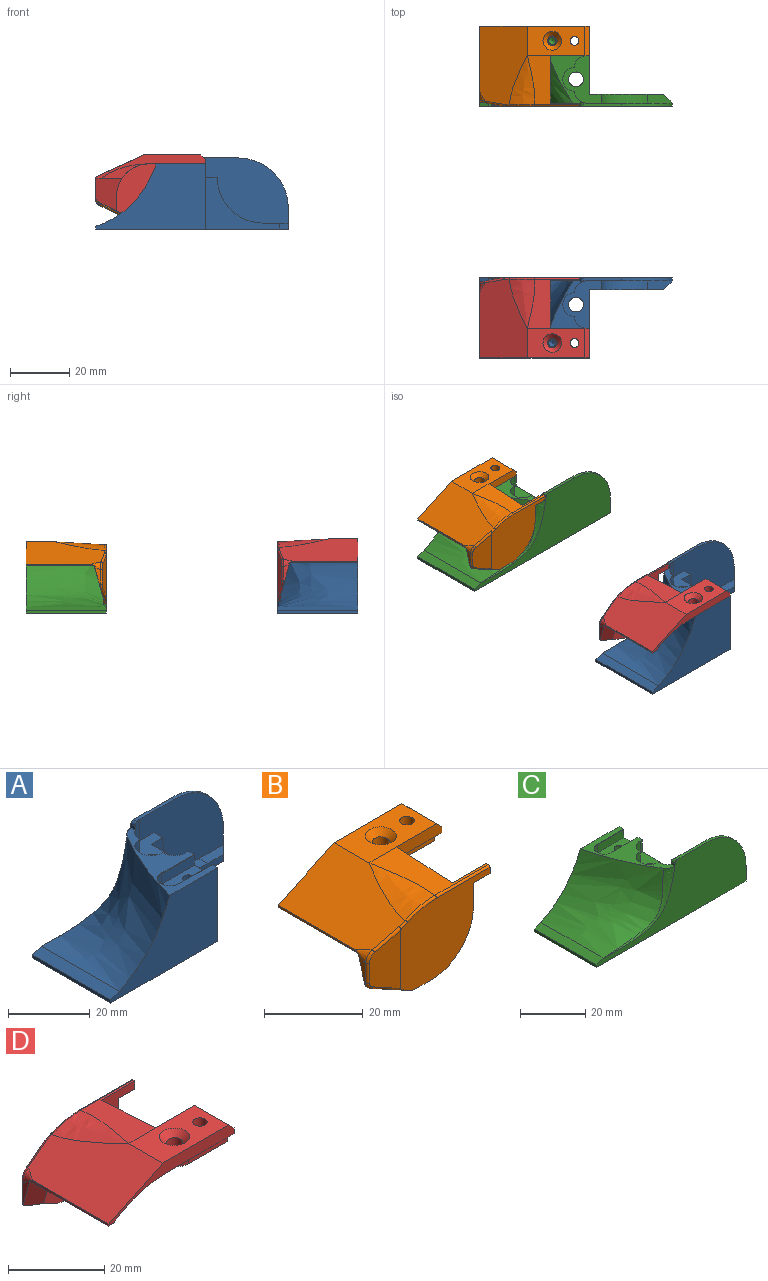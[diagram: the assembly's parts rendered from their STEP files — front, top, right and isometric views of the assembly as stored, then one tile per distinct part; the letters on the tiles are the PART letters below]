
ASSEMBLY  parts=4 mates=3
PART A: 37 faces, bbox 65.1x72.7x39.1 mm
  f0: plane 27.06x16.59mm, normal (0,0,1), area 125.5mm2, adj f3,f4,f10,f12,f14,f15,f16,f21
  f1: cylinder r=1.5mm len=18.8mm, axis (0,0,1), area 177.2mm2, adj f9,f26
  f2: plane 25x17.5mm, normal (0,-1,0), area 163.6mm2, adj f3,f9,f11,f17,f18,f19
  f3: plane 23x22mm, normal (1,0,0), area 428.3mm2, adj f0,f2,f4,f9,f11,f12,f26,f27
  f4: plane 37x22mm, normal (0,-1,0), area 528.7mm2, adj f0,f3,f7,f9,f21,f22
  f5: plane 65x24mm, normal (0,1,0), area 817.9mm2, adj f6,f7,f8,f9,f20,f22,f24,f25
  f6: plane 7x1mm, normal (1,0,0), area 7mm2, adj f5,f9,f13,f19,f20
  f7: plane 27x0.91mm, normal (-1,0,0), area 24.5mm2, adj f4,f5,f9,f22
  f8: plane 13x1.13mm, normal (0,0,1), area 13mm2, adj f5,f13,f14,f20,f25
  f9: plane 65x27mm, normal (0,0,-1), area 1079.8mm2, adj f1,f2,f3,f4,f5,f6,f7,f19
  f10: plane 1.54x1.01mm, normal (-1,0,0), area 1.5mm2, adj f0,f14,f24,f25
  f11: plane 16x13mm, normal (0,0,1), area 90.6mm2, adj f2,f3,f12,f13,f14,f15,f16,f17
  f12: plane 4.5x1mm, normal (0,1,0), area 4.5mm2, adj f0,f3,f11,f16
  f13: plane 29x22mm, normal (0,-1,0), area 446.9mm2, adj f6,f8,f11,f14,f17,f18,f20
  f14: cylinder r=4mm len=6.5mm, axis (0,0,1), area 31.9mm2, adj f0,f8,f10,f11,f13,f15,f25
  f15: cylinder r=4mm len=8mm, axis (0,0,1), area 56.5mm2, adj f0,f11,f14,f16
  f16: cylinder r=4mm len=4.5mm, axis (0,0,1), area 28.3mm2, adj f0,f11,f12,f15
  f17: cylinder r=15.5mm len=15.5mm, axis (0,-1,0), area 73mm2, adj f2,f11,f13,f18
  f18: plane 8.5x3mm, normal (0,0,1), area 21mm2, adj f2,f13,f17,f19
  f19: plane 3x3mm, normal (0.71,-0.71,0), area 8.5mm2, adj f2,f6,f9,f18
  f20: cylinder r=17mm len=17mm, axis (0,-1,0), area 26.7mm2, adj f5,f6,f8,f13
  f21: bspline ~72.59x37mm, area 910.9mm2, adj f0,f4,f22,f24
  f22: plane 27x3mm, normal (-0.34,0,0.94), area 86.2mm2, adj f4,f5,f7,f21
  f23: cylinder r=2.5mm len=17.5mm, axis (0,0,-1), area 274.9mm2, adj f9,f11
  f24: bspline ~31.79x24.78mm, area 59.9mm2, adj f0,f5,f10,f21,f25
  f25: cylinder r=1mm len=1.54mm, axis (0,-1,0), area 2.1mm2, adj f5,f8,f10,f14,f24
  f26: plane 14.5x6mm, normal (0,0,1), area 69mm2, adj f1,f3,f27,f28,f29,f33
  f27: plane 11.5x3.1mm, normal (0,1,0), area 35.6mm2, adj f3,f26,f29,f36
  f28: plane 11.5x3.1mm, normal (0,-1,0), area 35.6mm2, adj f3,f26,f29,f34
  f29: cylinder r=3mm len=6mm, axis (0,0,1), area 29.2mm2, adj f26,f27,f28,f35
  f30: cone r=1.25mm half-angle=59deg, axis (0,0,1), area 5.7mm2, adj f31
  f31: cylinder r=1.25mm len=2.5mm, axis (0,0,1), area 11.8mm2, adj f30,f32
  f32: plane 3x3mm, normal (0,0,1), area 2.2mm2, adj f31,f33
  f33: cylinder r=1.5mm len=3mm, axis (0,0,1), area 26.4mm2, adj f26,f32
  f34: plane 11.5x0.1mm, normal (0,-0.71,0.71), area 1.6mm2, adj f0,f3,f28,f35
  f35: cone r=3mm half-angle=45deg, axis (0,0,1), area 1.4mm2, adj f0,f29,f34,f36
  f36: plane 11.5x0.1mm, normal (0,0.71,0.71), area 1.6mm2, adj f0,f3,f27,f35
PART B: 47 faces, bbox 40x32.5x24 mm
  f0: plane 26x19.53mm, normal (0,0,-1), area 215.1mm2, adj f9,f10,f12,f14,f15,f17,f18,f19
  f1: plane 4.8x1mm, normal (0,0,-1), area 4.8mm2, adj f3,f11,f17,f34
  f2: plane 9.78x4.56mm, normal (-0.42,0,-0.91), area 3.7mm2, adj f17,f20,f30,f39
  f3: plane 6x1mm, normal (1,0,0), area 6mm2, adj f1,f4,f11,f17
  f4: cylinder r=12mm len=12mm, axis (0,-1,0), area 18.8mm2, adj f3,f5,f11,f17
  f5: plane 4.54x1mm, normal (0,0,-1), area 4.5mm2, adj f4,f11,f17,f39
  f6: plane 25.33x6.84mm, normal (-1,0,0), area 16.4mm2, adj f10,f13,f20,f23,f24,f28
  f7: plane 29.72x19.07mm, normal (-0.42,0,0.91), area 394.5mm2, adj f8,f10,f24,f25,f26,f37
  f8: plane 19.42x10mm, normal (0,0,1), area 155.9mm2, adj f7,f10,f19,f22,f31,f32,f35
  f9: plane 10x4.5mm, normal (1,0,0), area 33mm2, adj f0,f10,f19,f35,f41,f42,f43,f44
  f10: plane 37x8mm, normal (0,1,0), area 82.6mm2, adj f0,f6,f7,f8,f9,f12,f13,f35
  f11: plane 25.81x19.54mm, normal (0,-1,0), area 372.6mm2, adj f1,f3,f4,f5,f21,f26,f30,f34
  f12: cylinder r=28mm len=23mm, axis (0,1,0), area 390.8mm2, adj f0,f10,f13,f14
  f13: plane 23x1.5mm, normal (0,0,-1), area 34.5mm2, adj f6,f10,f12,f20
  f14: plane 16.5x5mm, normal (0,1,0), area 24.4mm2, adj f0,f12,f15,f20
  f15: cylinder r=11mm len=11mm, axis (0,1,0), area 46.5mm2, adj f0,f14,f16,f17,f20
  f16: plane 4.76x1.33mm, normal (1,0,0), area 3.2mm2, adj f15,f17,f20
  f17: plane 26.8x20.06mm, normal (0,1,0), area 353.9mm2, adj f0,f1,f2,f3,f4,f5,f15,f16
  f18: plane 16x3mm, normal (1,0,0), area 40.5mm2, adj f0,f17,f19,f22
  f19: plane 13x3mm, normal (0,-1,0), area 37.9mm2, adj f0,f8,f9,f18,f35
  f20: plane 10.84x8.85mm, normal (0,0.96,-0.27), area 69.6mm2, adj f2,f6,f13,f14,f15,f16,f23,f29
  f21: plane 14.23x7.5mm, normal (-0.17,-0.98,0), area 81.3mm2, adj f11,f26,f27,f28,f29,f30
  f22: plane 20.86x19.67mm, normal (0,-0.06,1), area 108.9mm2, adj f8,f17,f18,f25,f34,f36
  f23: cylinder r=2mm len=1.63mm, axis (0,-1,0), area 0.3mm2, adj f6,f20,f29
  f24: bspline ~25.59x2.72mm, area 5.2mm2, adj f6,f7,f27
  f25: bspline ~19.5x9.41mm, area 58.1mm2, adj f7,f22,f38
  f26: cylinder r=0.6mm len=6.82mm, axis (-0.89,0.16,-0.42), area 6.5mm2, adj f7,f11,f21,f27,f37
  f27: bspline ~2.7x1.97mm, area 2.5mm2, adj f21,f24,f26,f28
  f28: cylinder r=0.6mm len=4.9mm, axis (0,0,-1), area 4.1mm2, adj f6,f21,f27,f29
  f29: bspline ~2.23x1.42mm, area 1.7mm2, adj f20,f21,f23,f28,f30
  f30: cylinder r=0.6mm len=10.2mm, axis (0.89,-0.16,-0.42), area 8mm2, adj f2,f11,f20,f21,f29,f39
  f31: cylinder r=1.5mm len=6mm, axis (0,0,1), area 56.5mm2, adj f8,f43
  f32: cone r=3.15mm half-angle=45deg, axis (0,0,1), area 31.2mm2, adj f8,f33
  f33: cylinder r=1.7mm len=4.55mm, axis (0,0,1), area 48.6mm2, adj f32,f43
  f34: plane 2.06x1mm, normal (1,0,0), area 2mm2, adj f1,f11,f17,f22,f36
  f35: plane 10x1.5mm, normal (0.71,0,0.71), area 21.2mm2, adj f8,f9,f10,f19
  f36: cylinder r=0.5mm len=15.32mm, axis (-1,0,0), area 11.6mm2, adj f11,f22,f34,f38
  f37: cylinder r=0.5mm len=2.32mm, axis (-0.91,0,-0.42), area 1.6mm2, adj f7,f11,f26,f38
  f38: bspline ~8.57x2.36mm, area 6.8mm2, adj f11,f25,f36,f37
  f39: cylinder r=3mm len=1.27mm, axis (0,-1,0), area 1.3mm2, adj f2,f5,f11,f17,f30
  f40: cylinder r=3mm len=6mm, axis (0,0,1), area 27.3mm2, adj f0,f41,f42,f45
  f41: plane 11.5x2.9mm, normal (0,1,0), area 33.3mm2, adj f0,f9,f40,f44
  f42: plane 11.5x2.9mm, normal (0,-1,0), area 33.3mm2, adj f0,f9,f40,f46
  f43: plane 14.4x5.8mm, normal (0,0,-1), area 63.8mm2, adj f9,f31,f33,f44,f45,f46
  f44: plane 11.5x0.1mm, normal (0,0.71,-0.71), area 1.6mm2, adj f9,f41,f43,f45
  f45: cone r=2.9mm half-angle=45deg, axis (0,0,1), area 1.3mm2, adj f40,f43,f44,f46
  f46: plane 11.5x0.1mm, normal (0,-0.71,-0.71), area 1.6mm2, adj f9,f42,f43,f45
PART C: 37 faces, bbox 75.8x83.2x49.7 mm
  f0: cylinder r=1.5mm len=17.8mm, axis (0,0,1), area 167.8mm2, adj f8,f26
  f1: plane 25x16.5mm, normal (0,1,0), area 159.1mm2, adj f2,f8,f11,f17,f18,f19
  f2: plane 23x21mm, normal (1,0,0), area 405.3mm2, adj f1,f3,f8,f9,f11,f12,f26,f27
  f3: plane 47.79x31.81mm, normal (0,1,0), area 512mm2, adj f2,f6,f8,f9,f21,f22
  f4: plane 65x23mm, normal (0,-1,0), area 785.1mm2, adj f5,f6,f7,f8,f20,f22,f24,f25
  f5: plane 6x1mm, normal (1,0,0), area 6mm2, adj f4,f8,f13,f19,f20
  f6: plane 27x0.91mm, normal (-1,0,0), area 24.5mm2, adj f3,f4,f8,f22
  f7: plane 13x1.13mm, normal (0,0,1), area 13mm2, adj f4,f13,f14,f20,f25
  f8: plane 65x27mm, normal (0,0,-1), area 1079.8mm2, adj f0,f1,f2,f3,f4,f5,f6,f19
  f9: plane 31.5x21.41mm, normal (0,0,1), area 133.6mm2, adj f2,f3,f10,f12,f14,f15,f16,f21
  f10: plane 1.55x1.02mm, normal (-1,0,0), area 1.5mm2, adj f9,f14,f24,f25
  f11: plane 16x13mm, normal (0,0,1), area 90.6mm2, adj f1,f2,f12,f13,f14,f15,f16,f17
  f12: plane 4.5x1mm, normal (0,-1,0), area 4.5mm2, adj f2,f9,f11,f16
  f13: plane 29x21mm, normal (0,1,0), area 423.4mm2, adj f5,f7,f11,f14,f17,f18,f20
  f14: cylinder r=4mm len=6.5mm, axis (0,0,1), area 31.9mm2, adj f7,f9,f10,f11,f13,f15,f25
  f15: cylinder r=4mm len=8mm, axis (0,0,1), area 56.5mm2, adj f9,f11,f14,f16
  f16: cylinder r=4mm len=4.5mm, axis (0,0,1), area 28.3mm2, adj f9,f11,f12,f15
  f17: cylinder r=15.5mm len=15.47mm, axis (0,1,0), area 70mm2, adj f1,f11,f13,f18
  f18: plane 8.53x3mm, normal (0,0,1), area 21.1mm2, adj f1,f13,f17,f19
  f19: plane 3x3mm, normal (0.71,0.71,0), area 8.5mm2, adj f1,f5,f8,f18
  f20: cylinder r=17mm len=17mm, axis (0,1,0), area 26.7mm2, adj f4,f5,f7,f13
  f21: bspline ~72.4x36.9mm, area 726.6mm2, adj f3,f9,f22,f24
  f22: plane 27x3mm, normal (-0.34,0,0.94), area 86.2mm2, adj f3,f4,f6,f21
  f23: cylinder r=2.5mm len=16.5mm, axis (0,0,-1), area 259.2mm2, adj f8,f11
  f24: bspline ~31.68x23.74mm, area 57.8mm2, adj f4,f9,f10,f21,f25
  f25: cylinder r=1mm len=1.54mm, axis (0,1,0), area 2.1mm2, adj f4,f7,f10,f14,f24
  f26: plane 14.5x6mm, normal (0,0,1), area 69mm2, adj f0,f2,f27,f28,f29,f33
  f27: plane 11.5x3.1mm, normal (0,-1,0), area 35.6mm2, adj f2,f26,f28,f34
  f28: cylinder r=3mm len=6mm, axis (0,0,1), area 29.2mm2, adj f26,f27,f29,f35
  f29: plane 11.5x3.1mm, normal (0,1,0), area 35.6mm2, adj f2,f26,f28,f36
  f30: cone r=1.25mm half-angle=59deg, axis (0,0,1), area 5.7mm2, adj f31
  f31: cylinder r=1.25mm len=2.5mm, axis (0,0,1), area 11.8mm2, adj f30,f32
  f32: plane 3x3mm, normal (0,0,1), area 2.2mm2, adj f31,f33
  f33: cylinder r=1.5mm len=3mm, axis (0,0,1), area 26.4mm2, adj f26,f32
  f34: plane 11.5x0.1mm, normal (0,-0.71,0.71), area 1.6mm2, adj f2,f9,f27,f35
  f35: cone r=3mm half-angle=45deg, axis (0,0,1), area 1.4mm2, adj f9,f28,f34,f36
  f36: plane 11.5x0.1mm, normal (0,0.71,0.71), area 1.6mm2, adj f2,f9,f29,f35
PART D: 47 faces, bbox 40x32.5x24 mm
  f0: plane 4.8x1mm, normal (0,0,-1), area 4.8mm2, adj f2,f11,f17,f34
  f1: plane 9.78x4.56mm, normal (-0.42,0,-0.91), area 3.7mm2, adj f17,f20,f30,f39
  f2: plane 6x1mm, normal (1,0,0), area 6mm2, adj f0,f3,f11,f17
  f3: cylinder r=12mm len=12mm, axis (0,1,0), area 18.8mm2, adj f2,f4,f11,f17
  f4: plane 4.54x1mm, normal (0,0,-1), area 4.5mm2, adj f3,f11,f17,f39
  f5: plane 25.33x6.84mm, normal (-1,0,0), area 16.4mm2, adj f10,f13,f20,f23,f24,f28
  f6: plane 29.72x19.07mm, normal (-0.42,0,0.91), area 394.5mm2, adj f7,f10,f24,f25,f26,f37
  f7: plane 19.42x10mm, normal (0,0,1), area 155.9mm2, adj f6,f10,f19,f22,f31,f32,f35
  f8: plane 10x4.5mm, normal (1,0,0), area 33mm2, adj f9,f10,f19,f35,f40,f42,f43,f44
  f9: plane 26x19.53mm, normal (0,0,-1), area 215.1mm2, adj f8,f10,f12,f14,f15,f17,f18,f19
  f10: plane 37x8mm, normal (0,-1,0), area 82.6mm2, adj f5,f6,f7,f8,f9,f12,f13,f35
  f11: plane 25.81x19.54mm, normal (0,1,0), area 372.6mm2, adj f0,f2,f3,f4,f21,f26,f30,f34
  f12: cylinder r=28mm len=23mm, axis (0,-1,0), area 390.8mm2, adj f9,f10,f13,f14
  f13: plane 23x1.5mm, normal (0,0,-1), area 34.5mm2, adj f5,f10,f12,f20
  f14: plane 16.5x5mm, normal (0,-1,0), area 24.4mm2, adj f9,f12,f15,f20
  f15: cylinder r=11mm len=11mm, axis (0,-1,0), area 46.5mm2, adj f9,f14,f16,f17,f20
  f16: plane 4.76x1.33mm, normal (1,0,0), area 3.2mm2, adj f15,f17,f20
  f17: plane 26.8x20.06mm, normal (0,-1,0), area 353.9mm2, adj f0,f1,f2,f3,f4,f9,f15,f16
  f18: plane 16x3mm, normal (1,0,0), area 40.5mm2, adj f9,f17,f19,f22
  f19: plane 13x3mm, normal (0,1,0), area 37.9mm2, adj f7,f8,f9,f18,f35
  f20: plane 10.84x8.85mm, normal (0,-0.96,-0.27), area 69.6mm2, adj f1,f5,f13,f14,f15,f16,f23,f29
  f21: plane 14.23x7.5mm, normal (-0.17,0.98,0), area 81.3mm2, adj f11,f26,f27,f28,f29,f30
  f22: plane 20.86x19.67mm, normal (0,0.06,1), area 108.9mm2, adj f7,f17,f18,f25,f34,f36
  f23: cylinder r=2mm len=1.63mm, axis (0,1,0), area 0.3mm2, adj f5,f20,f29
  f24: bspline ~25.59x2.72mm, area 5.2mm2, adj f5,f6,f27
  f25: bspline ~19.5x9.41mm, area 58.1mm2, adj f6,f22,f38
  f26: cylinder r=0.6mm len=6.82mm, axis (-0.89,-0.16,-0.42), area 6.5mm2, adj f6,f11,f21,f27,f37
  f27: bspline ~2.7x1.97mm, area 2.5mm2, adj f21,f24,f26,f28
  f28: cylinder r=0.6mm len=4.9mm, axis (0,0,-1), area 4.1mm2, adj f5,f21,f27,f29
  f29: bspline ~2.23x1.42mm, area 1.7mm2, adj f20,f21,f23,f28,f30
  f30: cylinder r=0.6mm len=10.2mm, axis (0.89,0.16,-0.42), area 8mm2, adj f1,f11,f20,f21,f29,f39
  f31: cylinder r=1.5mm len=6mm, axis (0,0,1), area 56.5mm2, adj f7,f43
  f32: cone r=3.15mm half-angle=45deg, axis (0,0,1), area 31.2mm2, adj f7,f33
  f33: cylinder r=1.7mm len=4.55mm, axis (0,0,1), area 48.6mm2, adj f32,f43
  f34: plane 2.06x1mm, normal (1,0,0), area 2mm2, adj f0,f11,f17,f22,f36
  f35: plane 10x1.5mm, normal (0.71,0,0.71), area 21.2mm2, adj f7,f8,f10,f19
  f36: cylinder r=0.5mm len=15.32mm, axis (-1,0,0), area 11.6mm2, adj f11,f22,f34,f38
  f37: cylinder r=0.5mm len=2.32mm, axis (-0.91,0,-0.42), area 1.6mm2, adj f6,f11,f26,f38
  f38: bspline ~8.57x2.36mm, area 6.8mm2, adj f11,f25,f36,f37
  f39: cylinder r=3mm len=1.27mm, axis (0,1,0), area 1.3mm2, adj f1,f4,f11,f17,f30
  f40: plane 11.5x2.9mm, normal (0,-1,0), area 33.3mm2, adj f8,f9,f41,f44
  f41: cylinder r=3mm len=6mm, axis (0,0,1), area 27.3mm2, adj f9,f40,f42,f46
  f42: plane 11.5x2.9mm, normal (0,1,0), area 33.3mm2, adj f8,f9,f41,f45
  f43: plane 14.4x5.8mm, normal (0,0,-1), area 63.8mm2, adj f8,f31,f33,f44,f45,f46
  f44: plane 11.5x0.1mm, normal (0,-0.71,-0.71), area 1.6mm2, adj f8,f40,f43,f46
  f45: plane 11.5x0.1mm, normal (0,0.71,-0.71), area 1.6mm2, adj f8,f42,f43,f46
  f46: cone r=2.9mm half-angle=45deg, axis (0,0,1), area 1.3mm2, adj f41,f43,f44,f45
PLACE A t=(-17.54,24.21,-7.3)mm
PLACE B t=(-17.54,82.21,-4.3)mm
PLACE C t=(-17.54,82.21,-7.3)mm
PLACE D t=(-17.54,24.21,-3.3)mm
MATE fastened D.f8 <-> A.f3  axis (1,0,0) through (19.46,-2.79,14.7)mm
MATE fastened B.f9 <-> C.f2  axis (1,0,0) through (19.46,109.21,13.7)mm
MATE fastened C.f6 <-> A.f7  axis (-1,0,0) through (-17.54,82.21,-7.3)mm
